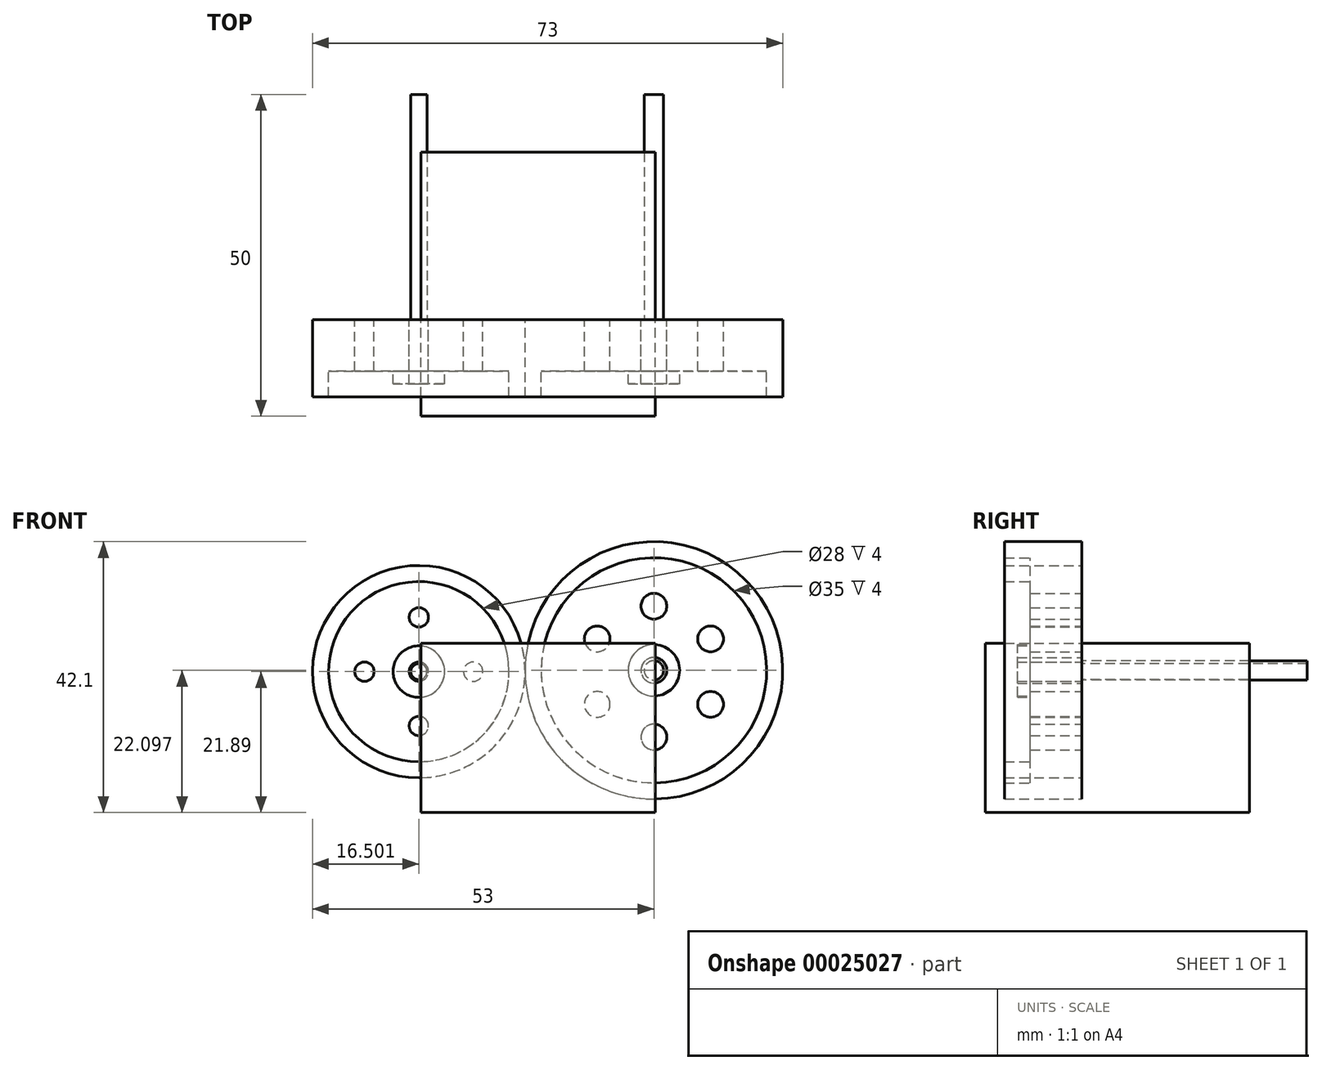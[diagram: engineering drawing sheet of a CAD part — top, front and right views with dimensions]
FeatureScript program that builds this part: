
annotation { "Feature Type Name" : "Feature", "Feature Type Description" : "" }
export const myFeature = defineFeature(function(context is Context, id is Id, definition is map)
    precondition{}
    {
        {
            var Q0;
            Q0=qCreatedBy(makeId("Front.planeOp"),FACE);
            var sketch = newSketch(context, id + "F0", { "sketchPlane" : qUnion([Q0])});
            skCircle(sketch, "E0", {"center": v(0, 0.2) * mm, "radius": 4 * mm});
            skCircle(sketch, "E1", {"center": v(0, 0.2) * mm, "radius": 17.5 * mm});
            skCircle(sketch, "E2", {"center": v(0, 0.2) * mm, "radius": 20 * mm});
            skLineSegment(sketch, "E3", {"start": v(0, 20.2) * mm, "end": v(0, -19.8) * mm});
            skLineSegment(sketch, "E4.anchor1", {"start": v(0, 12.07) * mm, "end": v(0, 0.2) * mm, "construction": true});
            skPoint(sketch, "E5.center", {"position": v(0, 0) * mm});
            skCircle(sketch, "E6.1.0", {"center": v(0, 0.2) * mm, "radius": 2 * mm});
            skCircle(sketch, "E7.1.0", {"center": v(0, -10.17) * mm, "radius": 2 * mm});
            skCircle(sketch, "E8.1.0", {"center": v(8.8, -5.08) * mm, "radius": 2 * mm});
            skCircle(sketch, "E8.2.0", {"center": v(8.8, 5.08) * mm, "radius": 2 * mm});
            skCircle(sketch, "E8.3.0", {"center": v(0, 10.17) * mm, "radius": 2 * mm});
            skCircle(sketch, "E8.4.0", {"center": v(-8.8, 5.08) * mm, "radius": 2 * mm});
            skCircle(sketch, "E8.5.0", {"center": v(-8.8, -5.08) * mm, "radius": 2 * mm});
            skCircle(sketch, "E9", {"center": v(-36.5, 0) * mm, "radius": 1.5 * mm});
            skCircle(sketch, "E10", {"center": v(-36.5, 0) * mm, "radius": 4 * mm});
            skCircle(sketch, "E11", {"center": v(-36.5, 0) * mm, "radius": 14 * mm});
            skPoint(sketch, "E12.trimOffspring.end.orphan", {"position": v(32.46, 52.78) * mm});
            skPoint(sketch, "E13.MirrorCS.start.orphan", {"position": v(-105.25, -16.92) * mm});
            skPoint(sketch, "E14.orphan", {"position": v(-30.8, 12.79) * mm});
            skCircle(sketch, "E15", {"center": v(-36.5, 0) * mm, "radius": 16.5 * mm});
            skLineSegment(sketch, "E16", {"start": v(-36.5, 0) * mm, "end": v(-36.5, -16.62) * mm});
            skCircle(sketch, "E17", {"center": v(-36.5, -8.45) * mm, "radius": 1.5 * mm});
            skCircle(sketch, "E18.1.0", {"center": v(-28.05, 0) * mm, "radius": 1.5 * mm});
            skCircle(sketch, "E18.2.0", {"center": v(-36.5, 8.45) * mm, "radius": 1.5 * mm});
            skCircle(sketch, "E18.3.0", {"center": v(-44.94, 0) * mm, "radius": 1.5 * mm});
            skSolve(sketch);
        }
        {
            var Q0;
            Q0=makeQuery(id+"F0.imprint","IMPRINT",FACE,{"disambiguationData":[TD([[makeQuery(id+"F0.imprint","IMPRINT",EDGE,{"derivedFrom":sQuery(id+"F0.wireOp",EDGE,"E4.4.0")}),-1.0]])]});
            var Q1;
            Q1=makeQuery(id+"F0.imprint","IMPRINT",FACE,{"disambiguationData":[TD([[makeQuery(id+"F0.imprint","IMPRINT",EDGE,{"derivedFrom":sQuery(id+"F0.wireOp",EDGE,"E4.1.0")}),-1.0]])]});
            var Q2;
            Q2=makeQuery(id+"F0.imprint","IMPRINT",FACE,{"disambiguationData":[TD([[makeQuery(id+"F0.imprint","IMPRINT",EDGE,{"derivedFrom":sQuery(id+"F0.wireOp",EDGE,"E8.4.0")}),-1.0]])]});
            var Q3;
            Q3=makeQuery(id+"F0.imprint","IMPRINT",FACE,{"disambiguationData":[TD([[makeQuery(id+"F0.imprint","IMPRINT",EDGE,{"derivedFrom":sQuery(id+"F0.wireOp",EDGE,"E8.1.0")}),-1.0]])]});
            extrude(context, id + "F1", {"entities" : qUnion([Q0, Q1, Q2, Q3]), "depth" : 8 * mm});
        }
        {
            var Q0;
            {var subQ1=sQuery(id+"F0.wireOp",EDGE,"E3");var subQ4=sQuery(id+"F0.wireOp",EDGE,"E0");var subQ6=makeQuery(id+"F0.imprint","INTERSECT",VERTEX,{"disambiguationData":[OD(0.0)],"derivedFrom":[subQ4,subQ1]});Q0=makeQuery(id+"F0.imprint","IMPRINT",FACE,{"disambiguationData":[TD([[makeQuery(id+"F0.imprint","IMPRINT",EDGE,{"disambiguationData":[TD([[subQ6,-1.0]])],"derivedFrom":subQ4}),1.0]])]});}
            var Q1;
            {var subQ0=sQuery(id+"F0.wireOp",EDGE,"E3");var subQ3=sQuery(id+"F0.wireOp",EDGE,"E0");var subQ6=makeQuery(id+"F0.imprint","INTERSECT",VERTEX,{"disambiguationData":[OD(0.0)],"derivedFrom":[subQ3,subQ0]});Q1=makeQuery(id+"F0.imprint","IMPRINT",FACE,{"disambiguationData":[TD([[makeQuery(id+"F0.imprint","IMPRINT",EDGE,{"disambiguationData":[TD([[subQ6,1.0]])],"derivedFrom":subQ3}),1.0]])]});}
            extrude(context, id + "F2", {"entities" : qUnion([Q0, Q1]), "operationType" : NewBodyOperationType.ADD, "depth" : 10 * mm});
        }
        {
            var Q0;
            {var subQ0=sQuery(id+"F0.wireOp",EDGE,"E3");var subQ1=sQuery(id+"F0.wireOp",EDGE,"E1");var subQ5=makeQuery(id+"F0.imprint","INTERSECT",VERTEX,{"disambiguationData":[OD(0.0)],"derivedFrom":[subQ1,subQ0]});Q0=makeQuery(id+"F0.imprint","IMPRINT",FACE,{"disambiguationData":[TD([[makeQuery(id+"F0.imprint","IMPRINT",EDGE,{"disambiguationData":[TD([[subQ5,-1.0]])],"derivedFrom":subQ1}),-1.0]])]});}
            var Q1;
            {var subQ0=sQuery(id+"F0.wireOp",EDGE,"E3");var subQ1=sQuery(id+"F0.wireOp",EDGE,"E1");var subQ5=makeQuery(id+"F0.imprint","INTERSECT",VERTEX,{"disambiguationData":[OD(0.0)],"derivedFrom":[subQ1,subQ0]});Q1=makeQuery(id+"F0.imprint","IMPRINT",FACE,{"disambiguationData":[TD([[makeQuery(id+"F0.imprint","IMPRINT",EDGE,{"disambiguationData":[TD([[subQ5,1.0]])],"derivedFrom":subQ1}),-1.0]])]});}
            extrude(context, id + "F3", {"entities" : qUnion([Q0, Q1]), "operationType" : NewBodyOperationType.ADD, "depth" : 12 * mm});
        }
        {
            var Q0;
            Q0=makeQuery(id+"F0.imprint","IMPRINT",FACE,{"disambiguationData":[TD([[makeQuery(id+"F0.imprint","IMPRINT",EDGE,{"derivedFrom":sQuery(id+"F0.wireOp",EDGE,"E11")}),-1.0]])]});
            extrude(context, id + "F4", {"entities" : qUnion([Q0]), "operationType" : NewBodyOperationType.ADD, "depth" : 12 * mm});
        }
        {
            var Q0;
            Q0=makeQuery(id+"F0.imprint","IMPRINT",FACE,{"disambiguationData":[TD([[makeQuery(id+"F0.imprint","IMPRINT",EDGE,{"derivedFrom":sQuery(id+"F0.wireOp",EDGE,"E10")}),-1.0]])]});
            extrude(context, id + "F5", {"entities" : qUnion([Q0]), "operationType" : NewBodyOperationType.ADD, "depth" : 8 * mm});
        }
        {
            var Q0;
            Q0=makeQuery(id+"F0.imprint","IMPRINT",FACE,{"disambiguationData":[TD([[makeQuery(id+"F0.imprint","IMPRINT",EDGE,{"derivedFrom":sQuery(id+"F0.wireOp",EDGE,"E9")}),-1.0]])]});
            extrude(context, id + "F6", {"entities" : qUnion([Q0]), "operationType" : NewBodyOperationType.ADD, "depth" : 10 * mm});
        }
        {
            var Q0;
            Q0=qCreatedBy(makeId("Front.planeOp"),FACE);
            var sketch = newSketch(context, id + "F7", { "sketchPlane" : qUnion([Q0])});
            skPoint(sketch, "E19.center", {"position": v(-36.5, 0) * mm});
            skCircle(sketch, "E20", {"center": v(-36.5, 0) * mm, "radius": 1.25 * mm});
            skCircle(sketch, "E21", {"center": v(0, 0.2) * mm, "radius": 1.5 * mm});
            skSolve(sketch);
        }
        {
            var Q0;
            Q0=makeQuery(id+"F7.imprint","IMPRINT",FACE,{"disambiguationData":[TD([[makeQuery(id+"F7.imprint","IMPRINT",EDGE,{"derivedFrom":sQuery(id+"F7.wireOp",EDGE,"E20")}),1.0]])]});
            extrude(context, id + "F8", {"entities" : qUnion([Q0]), "oppositeDirection" : true, "depth" : 35 * mm});
        }
        {
            var Q0;
            Q0=makeQuery(id+"F7.imprint","IMPRINT",FACE,{"disambiguationData":[TD([[makeQuery(id+"F7.imprint","IMPRINT",EDGE,{"derivedFrom":sQuery(id+"F7.wireOp",EDGE,"E21")}),1.0]])]});
            extrude(context, id + "F9", {"entities" : qUnion([Q0]), "oppositeDirection" : true, "depth" : 35 * mm});
        }
        {
            var Q0;
            Q0=qCreatedBy(makeId("Front.planeOp"),FACE);
            var sketch = newSketch(context, id + "F10", { "sketchPlane" : qUnion([Q0])});
            skLineSegment(sketch, "E22.bottom", {"start": v(-36.17, 4.43) * mm, "end": v(0.2, 4.43) * mm});
            skLineSegment(sketch, "E22.top", {"start": v(-36.17, -21.9) * mm, "end": v(0.2, -21.9) * mm});
            skLineSegment(sketch, "E22.left", {"start": v(-36.17, 4.43) * mm, "end": v(-36.17, -21.9) * mm});
            skLineSegment(sketch, "E22.right", {"start": v(0.2, 4.43) * mm, "end": v(0.2, -21.9) * mm});
            skSolve(sketch);
        }
        {
            var Q0;
            Q0 = qSketchRegion(id + "F10", true);
            extrude(context, id + "F11", {"entities" : qUnion([Q0]), "depth" : 15 * mm, "hasSecondDirection" : true, "secondDirectionOppositeDirection" : true, "secondDirectionDepth" : 26 * mm});
        }
    });
